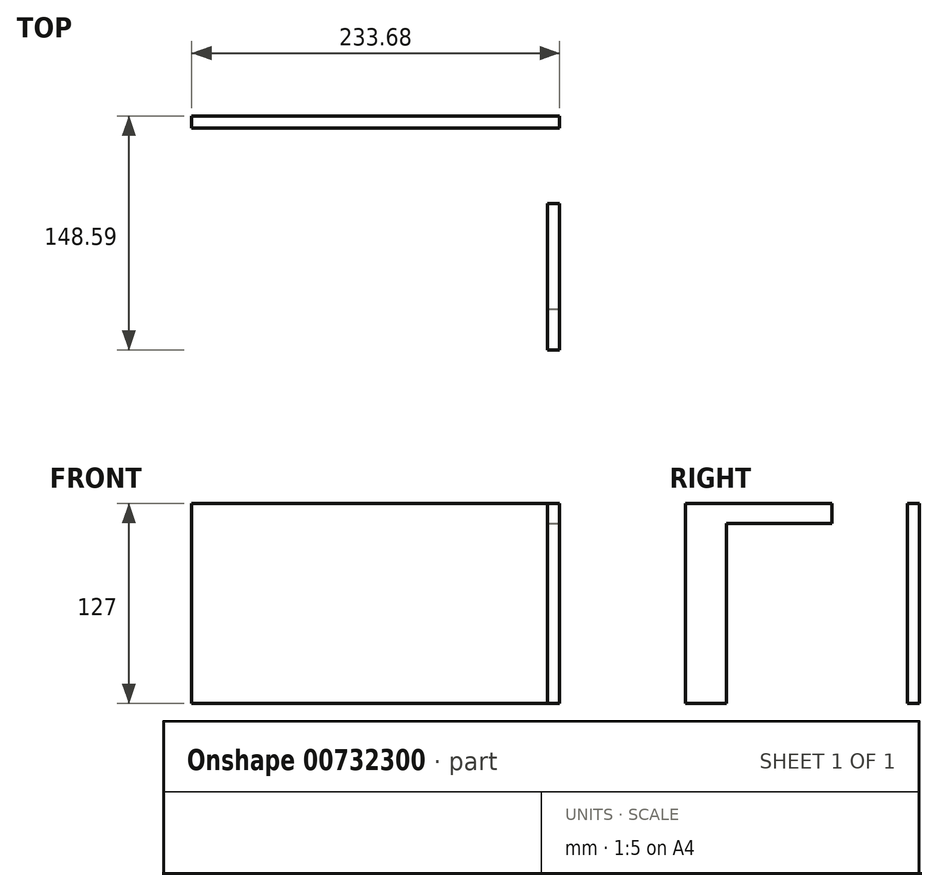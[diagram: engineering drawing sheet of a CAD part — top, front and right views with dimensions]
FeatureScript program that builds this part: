
annotation { "Feature Type Name" : "Feature", "Feature Type Description" : "" }
export const myFeature = defineFeature(function(context is Context, id is Id, definition is map)
    precondition{}
    {
        {
            var Q0;
            Q0=qCreatedBy(makeId("Top.planeOp"),FACE);
            var sketch = newSketch(context, id + "F0", { "sketchPlane" : qUnion([Q0])});
            skLineSegment(sketch, "E0.bottom", {"start": v(-111.97, 79.08) * mm, "end": v(121.7, 79.08) * mm});
            skLineSegment(sketch, "E0.top", {"start": v(-111.97, 71.46) * mm, "end": v(121.7, 71.46) * mm});
            skLineSegment(sketch, "E0.left", {"start": v(-111.97, 79.08) * mm, "end": v(-111.97, 71.46) * mm});
            skLineSegment(sketch, "E0.right", {"start": v(121.7, 79.08) * mm, "end": v(121.7, 71.46) * mm});
            skLineSegment(sketch, "E1.bottom", {"start": v(121.7, 71.46) * mm, "end": v(114.09, 71.46) * mm});
            skLineSegment(sketch, "E1.top", {"start": v(121.7, -69.5) * mm, "end": v(114.09, -69.5) * mm});
            skLineSegment(sketch, "E1.left", {"start": v(121.7, 71.46) * mm, "end": v(121.7, -69.5) * mm});
            skLineSegment(sketch, "E1.right", {"start": v(114.09, 71.46) * mm, "end": v(114.09, -69.5) * mm});
            skLineSegment(sketch, "E2.bottom", {"start": v(114.09, -43.6) * mm, "end": v(121.7, -43.6) * mm});
            skLineSegment(sketch, "E2.top", {"start": v(114.09, 23.38) * mm, "end": v(121.7, 23.38) * mm});
            skLineSegment(sketch, "E2.left", {"start": v(114.09, -43.6) * mm, "end": v(114.09, 23.38) * mm});
            skLineSegment(sketch, "E2.right", {"start": v(121.7, -43.6) * mm, "end": v(121.7, 23.38) * mm});
            skSolve(sketch);
        }
        {
            var Q0;
            Q0=makeQuery(id+"F0.imprint","IMPRINT",FACE,{"disambiguationData":[TD([[makeQuery(id+"F0.imprint","IMPRINT",EDGE,{"derivedFrom":sQuery(id+"F0.wireOp",EDGE,"E0.bottom")}),-1.0]])]});
            var Q1;
            Q1=makeQuery(id+"F0.imprint","IMPRINT",FACE,{"disambiguationData":[TD([[makeQuery(id+"F0.imprint","IMPRINT",EDGE,{"derivedFrom":sQuery(id+"F0.wireOp",EDGE,"E1.bottom")}),1.0]])]});
            extrude(context, id + "F1", {"entities" : qUnion([Q0, Q1]), "depth" : 127 * mm, "offsetDistance" : 25.4 * mm});
        }
        {
            var Q0;
            Q0=makeQuery(id+"F0.imprint","IMPRINT",FACE,{"disambiguationData":[TD([[makeQuery(id+"F0.imprint","IMPRINT",EDGE,{"derivedFrom":sQuery(id+"F0.wireOp",EDGE,"E2.bottom")}),1.0]])]});
            extrude(context, id + "F2", {"entities" : qUnion([Q0]), "operationType" : NewBodyOperationType.ADD, "depth" : 127 * mm, "offsetDistance" : 25.4 * mm});
        }
        {
            var Q0;
            Q0=makeQuery(id+"F0.imprint","IMPRINT",FACE,{"disambiguationData":[TD([[makeQuery(id+"F0.imprint","IMPRINT",EDGE,{"derivedFrom":sQuery(id+"F0.wireOp",EDGE,"E2.bottom")}),1.0]])]});
            extrude(context, id + "F3", {"entities" : qUnion([Q0]), "operationType" : NewBodyOperationType.REMOVE, "depth" : 114.3 * mm, "offsetDistance" : 25.4 * mm});
        }
        {
            var Q0;
            {var subQ0=sQuery(id+"F0.wireOp",EDGE,"E1.top");Q0=makeQuery(id+"F0.imprint","IMPRINT",FACE,{"disambiguationData":[TD([[makeQuery(id+"F0.imprint","IMPRINT",EDGE,{"derivedFrom":subQ0}),-1.0]])]});}
            extrude(context, id + "F4", {"entities" : qUnion([Q0]), "operationType" : NewBodyOperationType.ADD, "depth" : 127 * mm, "offsetDistance" : 25.4 * mm});
        }
    });
